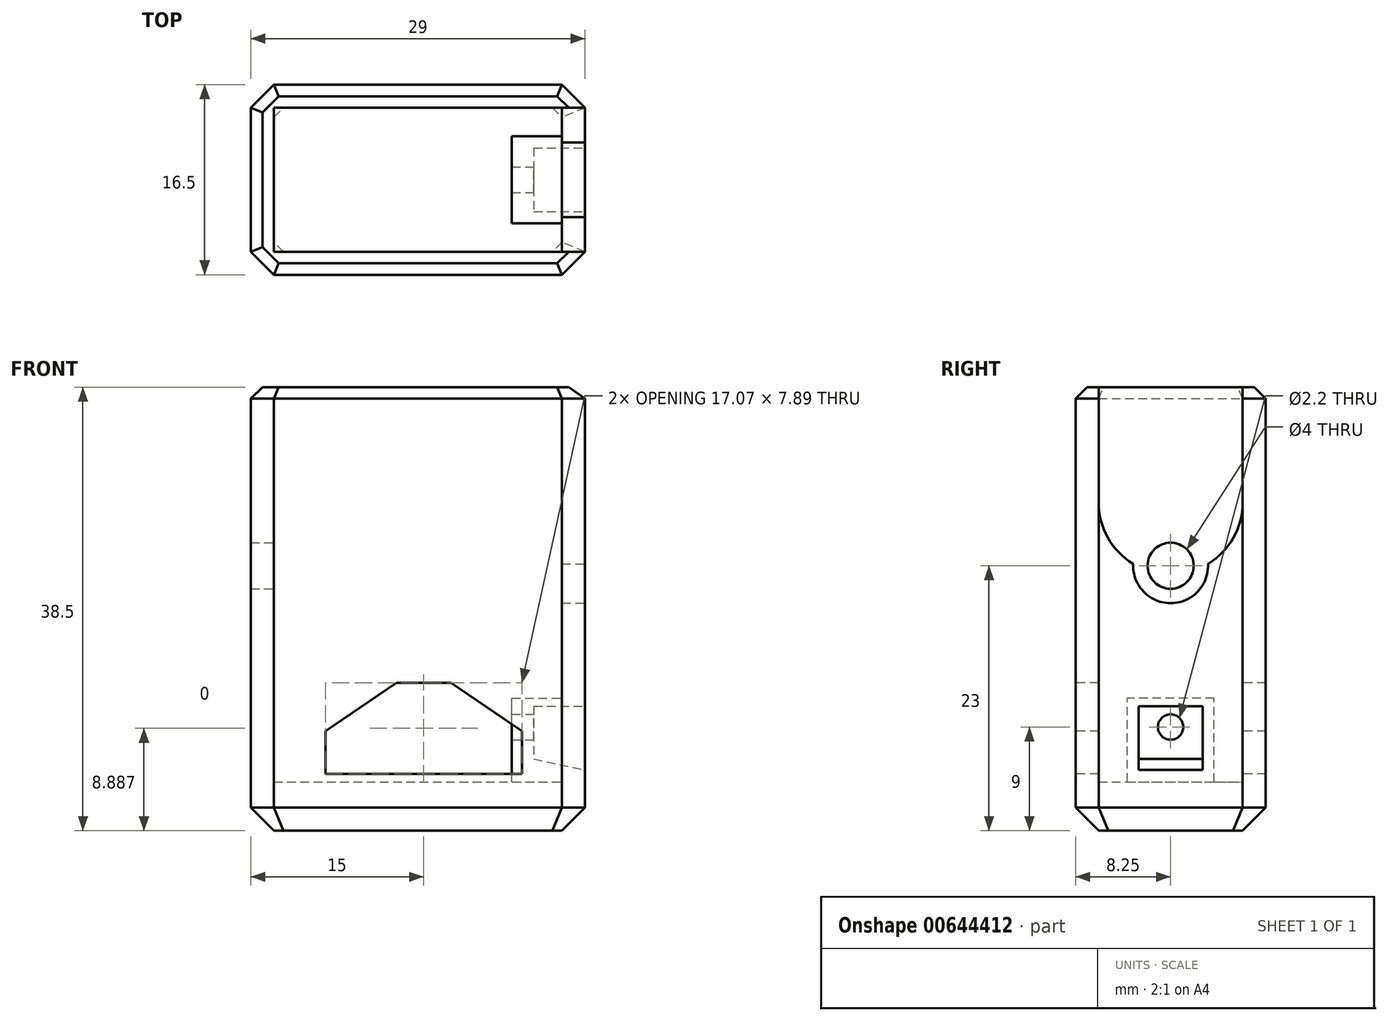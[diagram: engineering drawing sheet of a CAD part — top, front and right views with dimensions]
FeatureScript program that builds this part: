
annotation { "Feature Type Name" : "Feature", "Feature Type Description" : "" }
export const myFeature = defineFeature(function(context is Context, id is Id, definition is map)
    precondition{}
    {
        {
            var Q0;
            Q0=qCreatedBy(makeId("Top.planeOp"),FACE);
            var sketch = newSketch(context, id + "F0", { "sketchPlane" : qUnion([Q0])});
            skLineSegment(sketch, "E0.bottom", {"start": v(0, 0) * mm, "end": v(29, 0) * mm});
            skLineSegment(sketch, "E0.top", {"start": v(0, 16.5) * mm, "end": v(29, 16.5) * mm});
            skLineSegment(sketch, "E0.left", {"start": v(0, 0) * mm, "end": v(0, 16.5) * mm});
            skLineSegment(sketch, "E0.right", {"start": v(29, 0) * mm, "end": v(29, 16.5) * mm});
            skSolve(sketch);
        }
        {
            var Q0;
            Q0=qSketchRegion(id+"F0",true);
            extrude(context, id + "F1", {"entities" : qUnion([Q0]), "depth" : 38.5 * mm, "offsetDistance" : 25 * mm});
        }
        {
            var Q0;
            Q0=makeQuery(id+"F1.opExtrude","CAP_FACE",FACE,{"disambiguationData":[OSD([sQuery(id+"F0.wireOp",EDGE,"E0.bottom"),sQuery(id+"F0.wireOp",EDGE,"E0.top"),sQuery(id+"F0.wireOp",EDGE,"E0.left"),sQuery(id+"F0.wireOp",EDGE,"E0.right")])],"isStart":false});
            shell(context, id + "F2", {"entities" : qUnion([Q0]), "thickness" : 2 * mm});
        }
        {
            var Q0;
            Q0=makeQuery(id+"F2.opShell","OFFSET_FACE",FACE,{"disambiguationData":[OSD([sQuery(id+"F0.wireOp",EDGE,"E0.bottom"),sQuery(id+"F0.wireOp",EDGE,"E0.top"),sQuery(id+"F0.wireOp",EDGE,"E0.left"),sQuery(id+"F0.wireOp",EDGE,"E0.right")])]});
            extrude(context, id + "F3", {"entities" : qUnion([Q0]), "operationType" : NewBodyOperationType.ADD, "depth" : 2.25 * mm, "offsetDistance" : 25 * mm});
        }
        {
            var Q0;
            Q0=makeQuery(id+"F1.opExtrude","SWEPT_EDGE",EDGE,{"disambiguationData":[OSD([sQuery(id+"F0.wireOp",EDGE,"E0.bottom"),sQuery(id+"F0.wireOp",EDGE,"E0.right")])]});
            var Q1;
            Q1=makeQuery(id+"F1.opExtrude","SWEPT_EDGE",EDGE,{"disambiguationData":[OSD([sQuery(id+"F0.wireOp",EDGE,"E0.bottom"),sQuery(id+"F0.wireOp",EDGE,"E0.left")])]});
            var Q2;
            Q2=makeQuery(id+"F1.opExtrude","SWEPT_EDGE",EDGE,{"disambiguationData":[OSD([sQuery(id+"F0.wireOp",EDGE,"E0.top"),sQuery(id+"F0.wireOp",EDGE,"E0.right")])]});
            var Q3;
            Q3=makeQuery(id+"F1.opExtrude","SWEPT_EDGE",EDGE,{"disambiguationData":[OSD([sQuery(id+"F0.wireOp",EDGE,"E0.top"),sQuery(id+"F0.wireOp",EDGE,"E0.left")])]});
            chamfer(context, id + "F4", {"entities" : qUnion([Q0, Q1, Q2, Q3]), "width" : 2 * mm, "tangentPropagation" : true});
        }
        {
            var Q0;
            Q0=makeQuery(id+"F1.opExtrude","CAP_FACE",FACE,{"disambiguationData":[OSD([sQuery(id+"F0.wireOp",EDGE,"E0.bottom"),sQuery(id+"F0.wireOp",EDGE,"E0.top"),sQuery(id+"F0.wireOp",EDGE,"E0.left"),sQuery(id+"F0.wireOp",EDGE,"E0.right")])],"isStart":true});
            chamfer(context, id + "F5", {"entities" : qUnion([Q0]), "width" : 2 * mm, "tangentPropagation" : true});
        }
        {
            var Q0;
            Q0=makeQuery(id+"F1.opExtrude","CAP_EDGE",EDGE,{"disambiguationData":[OSD([sQuery(id+"F0.wireOp",EDGE,"E0.bottom")])],"isStart":false});
            var Q1;
            {var subQ0=sQuery(id+"F0.wireOp",EDGE,"E0.left");var subQ1=sQuery(id+"F0.wireOp",EDGE,"E0.bottom");Q1=makeQuery(id+"F4.opChamfer","BLEND_EDGE",EDGE,{"blendedFrom":[makeQuery(id+"F1.opExtrude","SWEPT_EDGE",EDGE,{"disambiguationData":[OSD([subQ1,subQ0])]}),makeQuery(id+"F1.opExtrude","CAP_FACE",FACE,{"disambiguationData":[OSD([subQ1,sQuery(id+"F0.wireOp",EDGE,"E0.top"),subQ0,sQuery(id+"F0.wireOp",EDGE,"E0.right")])],"isStart":false})],"blendedInto":[makeQuery(id+"F1.opExtrude","CAP_FACE",FACE,{"disambiguationData":[OSD([subQ1,sQuery(id+"F0.wireOp",EDGE,"E0.top"),subQ0,sQuery(id+"F0.wireOp",EDGE,"E0.right")])],"isStart":false})]});}
            var Q2;
            Q2=makeQuery(id+"F1.opExtrude","CAP_EDGE",EDGE,{"disambiguationData":[OSD([sQuery(id+"F0.wireOp",EDGE,"E0.left")])],"isStart":false});
            var Q3;
            {var subQ0=sQuery(id+"F0.wireOp",EDGE,"E0.left");var subQ1=sQuery(id+"F0.wireOp",EDGE,"E0.top");Q3=makeQuery(id+"F4.opChamfer","BLEND_EDGE",EDGE,{"blendedFrom":[makeQuery(id+"F1.opExtrude","SWEPT_EDGE",EDGE,{"disambiguationData":[OSD([subQ1,subQ0])]}),makeQuery(id+"F1.opExtrude","CAP_FACE",FACE,{"disambiguationData":[OSD([sQuery(id+"F0.wireOp",EDGE,"E0.bottom"),subQ1,subQ0,sQuery(id+"F0.wireOp",EDGE,"E0.right")])],"isStart":false})],"blendedInto":[makeQuery(id+"F1.opExtrude","CAP_FACE",FACE,{"disambiguationData":[OSD([sQuery(id+"F0.wireOp",EDGE,"E0.bottom"),subQ1,subQ0,sQuery(id+"F0.wireOp",EDGE,"E0.right")])],"isStart":false})]});}
            var Q4;
            Q4=makeQuery(id+"F1.opExtrude","CAP_EDGE",EDGE,{"disambiguationData":[OSD([sQuery(id+"F0.wireOp",EDGE,"E0.top")])],"isStart":false});
            var Q5;
            {var subQ0=sQuery(id+"F0.wireOp",EDGE,"E0.right");var subQ1=sQuery(id+"F0.wireOp",EDGE,"E0.top");Q5=makeQuery(id+"F4.opChamfer","BLEND_EDGE",EDGE,{"blendedFrom":[makeQuery(id+"F1.opExtrude","SWEPT_EDGE",EDGE,{"disambiguationData":[OSD([subQ1,subQ0])]}),makeQuery(id+"F1.opExtrude","CAP_FACE",FACE,{"disambiguationData":[OSD([sQuery(id+"F0.wireOp",EDGE,"E0.bottom"),subQ1,sQuery(id+"F0.wireOp",EDGE,"E0.left"),subQ0])],"isStart":false})],"blendedInto":[makeQuery(id+"F1.opExtrude","CAP_FACE",FACE,{"disambiguationData":[OSD([sQuery(id+"F0.wireOp",EDGE,"E0.bottom"),subQ1,sQuery(id+"F0.wireOp",EDGE,"E0.left"),subQ0])],"isStart":false})]});}
            var Q6;
            Q6=makeQuery(id+"F1.opExtrude","CAP_EDGE",EDGE,{"disambiguationData":[OSD([sQuery(id+"F0.wireOp",EDGE,"E0.right")])],"isStart":false});
            var Q7;
            {var subQ0=sQuery(id+"F0.wireOp",EDGE,"E0.right");var subQ1=sQuery(id+"F0.wireOp",EDGE,"E0.bottom");Q7=makeQuery(id+"F4.opChamfer","BLEND_EDGE",EDGE,{"blendedFrom":[makeQuery(id+"F1.opExtrude","SWEPT_EDGE",EDGE,{"disambiguationData":[OSD([subQ1,subQ0])]}),makeQuery(id+"F1.opExtrude","CAP_FACE",FACE,{"disambiguationData":[OSD([subQ1,sQuery(id+"F0.wireOp",EDGE,"E0.top"),sQuery(id+"F0.wireOp",EDGE,"E0.left"),subQ0])],"isStart":false})],"blendedInto":[makeQuery(id+"F1.opExtrude","CAP_FACE",FACE,{"disambiguationData":[OSD([subQ1,sQuery(id+"F0.wireOp",EDGE,"E0.top"),sQuery(id+"F0.wireOp",EDGE,"E0.left"),subQ0])],"isStart":false})]});}
            chamfer(context, id + "F6", {"entities" : qUnion([Q0, Q1, Q2, Q3, Q4, Q5, Q6, Q7]), "width" : 1 * mm, "tangentPropagation" : true});
        }
        {
            var Q0;
            Q0=makeQuery(id+"F1.opExtrude","SWEPT_FACE",FACE,{"disambiguationData":[OSD([sQuery(id+"F0.wireOp",EDGE,"E0.bottom")])]});
            var sketch = newSketch(context, id + "F7", { "sketchPlane" : qUnion([Q0])});
            skLineSegment(sketch, "E1", {"start": v(6.46, 4.94) * mm, "end": v(23.54, 4.94) * mm});
            skLineSegment(sketch, "E2", {"start": v(23.54, 4.94) * mm, "end": v(23.54, 8.66) * mm});
            skLineSegment(sketch, "E3", {"start": v(23.54, 8.66) * mm, "end": v(17.36, 12.83) * mm});
            skLineSegment(sketch, "E4", {"start": v(17.36, 12.83) * mm, "end": v(12.63, 12.83) * mm});
            skLineSegment(sketch, "E5", {"start": v(12.63, 12.83) * mm, "end": v(6.46, 8.66) * mm});
            skLineSegment(sketch, "E6", {"start": v(6.46, 8.66) * mm, "end": v(6.46, 4.94) * mm});
            skSolve(sketch);
        }
        {
            var Q0;
            Q0=makeQuery(id+"F7.imprint","IMPRINT",FACE,{"disambiguationData":[TD([[makeQuery(id+"F7.imprint","IMPRINT",EDGE,{"derivedFrom":sQuery(id+"F7.wireOp",EDGE,"E1")}),1.0]])]});
            extrude(context, id + "F8", {"entities" : qUnion([Q0]), "operationType" : NewBodyOperationType.REMOVE, "endBound" : BoundingType.THROUGH_ALL, "oppositeDirection" : true, "depth" : 25 * mm, "offsetDistance" : 25 * mm});
        }
        {
            var Q0;
            Q0=makeQuery(id+"F1.opExtrude","SWEPT_FACE",FACE,{"disambiguationData":[OSD([sQuery(id+"F0.wireOp",EDGE,"E0.right")])]});
            var sketch = newSketch(context, id + "F9", { "sketchPlane" : qUnion([Q0])});
            skCircle(sketch, "E7", {"center": v(8.25, 23) * mm, "radius": 3.25 * mm});
            skCircle(sketch, "E8", {"center": v(8.25, 28.5) * mm, "radius": 6.25 * mm});
            skLineSegment(sketch, "E9.bottom", {"start": v(2, 28.5) * mm, "end": v(14.5, 28.5) * mm});
            skLineSegment(sketch, "E9.top", {"start": v(2, 38.5) * mm, "end": v(14.5, 38.5) * mm});
            skLineSegment(sketch, "E9.left", {"start": v(2, 28.5) * mm, "end": v(2, 38.5) * mm});
            skLineSegment(sketch, "E9.right", {"start": v(14.5, 28.5) * mm, "end": v(14.5, 38.5) * mm});
            skSolve(sketch);
        }
        {
            var Q0;
            {var subQ0=sQuery(id+"F9.wireOp",EDGE,"E8");var subQ1=sQuery(id+"F9.wireOp",EDGE,"E7");var subQ2=makeQuery(id+"F9.imprint","INTERSECT",VERTEX,{"disambiguationData":[OD(0.0)],"derivedFrom":[subQ1,subQ0]});Q0=makeQuery(id+"F9.imprint","IMPRINT",FACE,{"disambiguationData":[TD([[makeQuery(id+"F9.imprint","IMPRINT",EDGE,{"disambiguationData":[TD([[subQ2,-1.0]])],"derivedFrom":subQ1}),1.0]])]});}
            var Q1;
            {var subQ0=sQuery(id+"F9.wireOp",EDGE,"E8");var subQ1=sQuery(id+"F9.wireOp",EDGE,"E7");var subQ2=makeQuery(id+"F9.imprint","INTERSECT",VERTEX,{"disambiguationData":[OD(0.0)],"derivedFrom":[subQ1,subQ0]});Q1=makeQuery(id+"F9.imprint","IMPRINT",FACE,{"disambiguationData":[TD([[makeQuery(id+"F9.imprint","IMPRINT",EDGE,{"disambiguationData":[TD([[subQ2,1.0]])],"derivedFrom":subQ1}),1.0]])]});}
            var Q2;
            {var subQ4=sQuery(id+"F9.wireOp",EDGE,"E9.bottom");Q2=makeQuery(id+"F9.imprint","IMPRINT",FACE,{"disambiguationData":[TD([[makeQuery(id+"F9.imprint","IMPRINT",EDGE,{"derivedFrom":subQ4}),-1.0]])]});}
            var Q3;
            {var subQ0=sQuery(id+"F9.wireOp",EDGE,"E9.bottom");Q3=makeQuery(id+"F9.imprint","IMPRINT",FACE,{"disambiguationData":[TD([[makeQuery(id+"F9.imprint","IMPRINT",EDGE,{"derivedFrom":subQ0}),1.0]])]});}
            var Q4;
            {var subQ3=sQuery(id+"F0.wireOp",EDGE,"E0.right");var subQ4=makeQuery(id+"F1.opExtrude","SWEPT_FACE",FACE,{"disambiguationData":[OSD([subQ3])]});var subQ8=makeQuery(id+"F6.opChamfer","BLEND_EDGE",EDGE,{"blendedFrom":[makeQuery(id+"F1.opExtrude","CAP_EDGE",EDGE,{"disambiguationData":[OSD([subQ3])],"isStart":false}),subQ4],"blendedInto":[subQ4]});Q4=makeQuery(id+"F9.imprint","IMPRINT",FACE,{"disambiguationData":[TD([[makeQuery(id+"F9.imprint","IMPRINT",EDGE,{"derivedFrom":subQ8}),1.0]])]});}
            var Q5;
            {var subQ0=sQuery(id+"F9.wireOp",EDGE,"E9.top");Q5=makeQuery(id+"F9.imprint","IMPRINT",FACE,{"disambiguationData":[TD([[makeQuery(id+"F9.imprint","IMPRINT",EDGE,{"derivedFrom":subQ0}),-1.0]])]});}
            extrude(context, id + "F10", {"entities" : qUnion([Q0, Q1, Q2, Q3, Q4, Q5]), "operationType" : NewBodyOperationType.REMOVE, "endBound" : BoundingType.UP_TO_NEXT, "oppositeDirection" : true, "depth" : 25 * mm, "offsetDistance" : 25 * mm});
        }
        {
            var Q0;
            Q0=makeQuery(id+"F2.opShell","OFFSET_FACE",FACE,{"disambiguationData":[OSD([sQuery(id+"F0.wireOp",EDGE,"E0.left")])]});
            var sketch = newSketch(context, id + "F11", { "sketchPlane" : qUnion([Q0])});
            skCircle(sketch, "E10", {"center": v(8.25, 23) * mm, "radius": 2 * mm});
            skSolve(sketch);
        }
        {
            var Q0;
            Q0=makeQuery(id+"F11.imprint","IMPRINT",FACE,{"disambiguationData":[TD([[makeQuery(id+"F11.imprint","IMPRINT",EDGE,{"derivedFrom":sQuery(id+"F11.wireOp",EDGE,"E10")}),1.0]])]});
            extrude(context, id + "F12", {"entities" : qUnion([Q0]), "operationType" : NewBodyOperationType.REMOVE, "endBound" : BoundingType.THROUGH_ALL, "oppositeDirection" : true, "depth" : 25 * mm, "offsetDistance" : 25 * mm});
        }
        {
            var Q0;
            Q0=makeQuery(id+"F2.opShell","OFFSET_FACE",FACE,{"disambiguationData":[OSD([sQuery(id+"F0.wireOp",EDGE,"E0.right")])]});
            var sketch = newSketch(context, id + "F13", { "sketchPlane" : qUnion([Q0])});
            skLineSegment(sketch, "E11.bottom", {"start": v(-12.02, 4.25) * mm, "end": v(-4.48, 4.25) * mm});
            skLineSegment(sketch, "E11.top", {"start": v(-12.02, 11.5) * mm, "end": v(-4.48, 11.5) * mm});
            skLineSegment(sketch, "E11.left", {"start": v(-12.02, 4.25) * mm, "end": v(-12.02, 11.5) * mm});
            skLineSegment(sketch, "E11.right", {"start": v(-4.48, 4.25) * mm, "end": v(-4.48, 11.5) * mm});
            skCircle(sketch, "E12", {"center": v(-8.25, 9) * mm, "radius": 1.1 * mm});
            skSolve(sketch);
        }
        {
            var Q0;
            Q0 = qSketchRegion(id + "F13", true);
            extrude(context, id + "F14", {"entities" : qUnion([Q0]), "operationType" : NewBodyOperationType.ADD, "depth" : 4.35 * mm, "offsetDistance" : 25 * mm});
        }
        {
            var Q0;
            Q0=makeQuery(id+"F1.opExtrude","SWEPT_FACE",FACE,{"disambiguationData":[OSD([sQuery(id+"F0.wireOp",EDGE,"E0.right")])]});
            var sketch = newSketch(context, id + "F15", { "sketchPlane" : qUnion([Q0])});
            skLineSegment(sketch, "E13.bottom", {"start": v(5.48, 5.27) * mm, "end": v(11.02, 5.27) * mm});
            skLineSegment(sketch, "E13.top", {"start": v(5.48, 10.8) * mm, "end": v(11.02, 10.8) * mm});
            skLineSegment(sketch, "E13.left", {"start": v(5.48, 5.27) * mm, "end": v(5.48, 10.8) * mm});
            skLineSegment(sketch, "E13.right", {"start": v(11.02, 5.27) * mm, "end": v(11.02, 10.8) * mm});
            skSolve(sketch);
        }
        {
            var Q0;
            Q0=makeQuery(id+"F15.imprint","IMPRINT",FACE,{"disambiguationData":[TD([[makeQuery(id+"F15.imprint","IMPRINT",EDGE,{"derivedFrom":sQuery(id+"F15.wireOp",EDGE,"E13.bottom")}),-1.0]])]});
            cPlane(context, id + "F16", {"entities" : qUnion([Q0]), "cplaneType" : CPlaneType.OFFSET, "offset" : 4.45 * mm, "oppositeDirection" : true, "width" : 150 * mm, "height" : 150 * mm});
        }
        {
            var Q0;
            Q0=qCreatedBy(id+"F16.planeOp",FACE);
            var sketch = newSketch(context, id + "F17", { "sketchPlane" : qUnion([Q0])});
            skLineSegment(sketch, "E14.bottom", {"start": v(11.02, 10.8) * mm, "end": v(5.48, 10.8) * mm});
            skLineSegment(sketch, "E14.top", {"start": v(11.02, 6.22) * mm, "end": v(5.48, 6.22) * mm});
            skLineSegment(sketch, "E14.left", {"start": v(11.02, 10.8) * mm, "end": v(11.02, 6.22) * mm});
            skLineSegment(sketch, "E14.right", {"start": v(5.48, 10.8) * mm, "end": v(5.48, 6.22) * mm});
            skSolve(sketch);
        }
        {
            var Q1;
            Q1=qSketchRegion(id+"F17",true);
            var Q2;
            Q2=qSketchRegion(id+"F15",true);
            loft(context, id + "F18", {"operationType" : NewBodyOperationType.REMOVE, "sheetProfilesArray" : [{ "sheetProfileEntities" : qUnion([Q1]) }, { "sheetProfileEntities" : qUnion([Q2]) }]});
        }
    });
